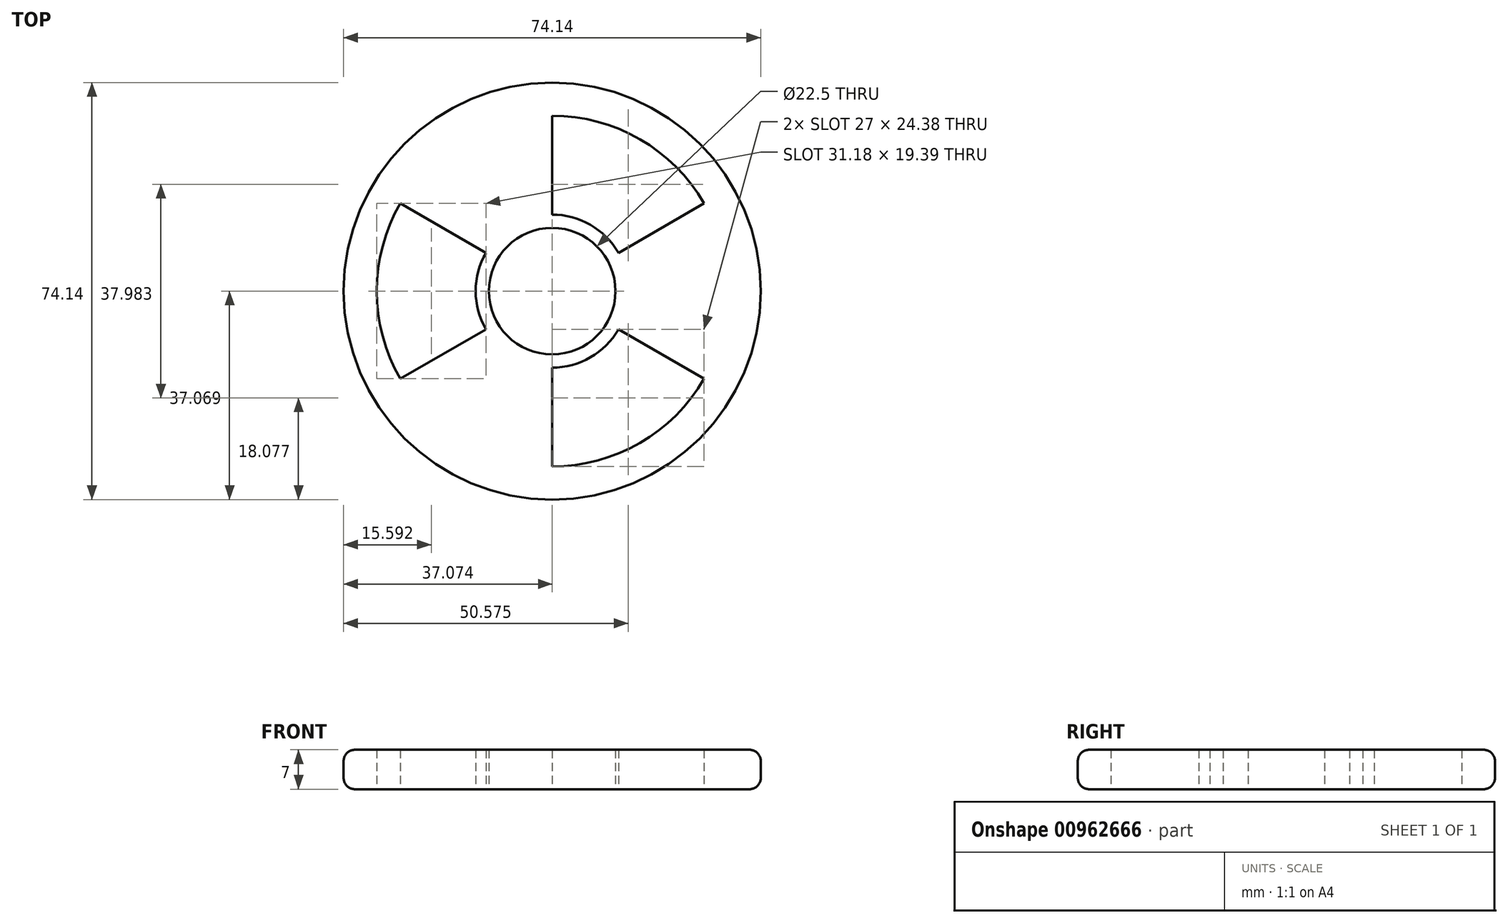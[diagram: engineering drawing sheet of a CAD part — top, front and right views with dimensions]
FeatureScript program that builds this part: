
annotation { "Feature Type Name" : "Feature", "Feature Type Description" : "" }
export const myFeature = defineFeature(function(context is Context, id is Id, definition is map)
    precondition{}
    {
        {
            var Q0;
            Q0=qCreatedBy(makeId("Top.planeOp"),FACE);
            var sketch = newSketch(context, id + "F0", { "sketchPlane" : qUnion([Q0])});
            skCircle(sketch, "E0", {"center": v(-44.39, -7.32) * mm, "radius": 11.25 * mm});
            skCircle(sketch, "E1", {"center": v(-44.39, -7.32) * mm, "radius": 37.07 * mm});
            skCircle(sketch, "E2", {"center": v(-44.39, -7.32) * mm, "radius": 31.18 * mm});
            skCircle(sketch, "E3", {"center": v(-44.39, -7.32) * mm, "radius": 13.6 * mm});
            skLineSegment(sketch, "E4", {"start": v(-44.39, 6.29) * mm, "end": v(-44.39, 23.86) * mm});
            skLineSegment(sketch, "E5.1.0", {"start": v(-56.17, -0.52) * mm, "end": v(-71.39, 8.27) * mm});
            skLineSegment(sketch, "E5.2.0", {"start": v(-56.17, -14.13) * mm, "end": v(-71.39, -22.91) * mm});
            skLineSegment(sketch, "E5.3.0", {"start": v(-44.39, -20.93) * mm, "end": v(-44.39, -38.5) * mm});
            skLineSegment(sketch, "E5.4.0", {"start": v(-32.6, -14.13) * mm, "end": v(-17.38, -22.91) * mm});
            skLineSegment(sketch, "E5.5.0", {"start": v(-32.6, -0.52) * mm, "end": v(-17.38, 8.27) * mm});
            skSolve(sketch);
        }
        {
            var Q0;
            Q0 = qSketchRegion(id + "F0", true);
            var Q1;
            Q1=makeQuery(id+"F0.imprint","IMPRINT",FACE,{"disambiguationData":[TD([[makeQuery(id+"F0.imprint","IMPRINT",EDGE,{"derivedFrom":sQuery(id+"F0.wireOp",EDGE,"E0")}),-1.0]])]});
            var Q2;
            {var subQ0=sQuery(id+"F0.wireOp",EDGE,"E5.2.0");Q2=makeQuery(id+"F0.imprint","IMPRINT",FACE,{"disambiguationData":[TD([[makeQuery(id+"F0.imprint","IMPRINT",EDGE,{"derivedFrom":subQ0}),1.0]])]});}
            var Q3;
            {var subQ0=sQuery(id+"F0.wireOp",EDGE,"E4");Q3=makeQuery(id+"F0.imprint","IMPRINT",FACE,{"disambiguationData":[TD([[makeQuery(id+"F0.imprint","IMPRINT",EDGE,{"derivedFrom":subQ0}),1.0]])]});}
            var Q4;
            {var subQ0=sQuery(id+"F0.wireOp",EDGE,"E5.4.0");Q4=makeQuery(id+"F0.imprint","IMPRINT",FACE,{"disambiguationData":[TD([[makeQuery(id+"F0.imprint","IMPRINT",EDGE,{"derivedFrom":subQ0}),1.0]])]});}
            extrude(context, id + "F1", {"entities" : qUnion([Q0, Q1, Q2, Q3, Q4]), "depth" : 7 * mm, "offsetDistance" : 25 * mm});
        }
        {
            var Q0;
            Q0=makeQuery(id+"F1.opExtrude","CAP_EDGE",EDGE,{"disambiguationData":[OSD([sQuery(id+"F0.wireOp",EDGE,"E1")])],"isStart":true});
            var Q1;
            Q1=makeQuery(id+"F1.opExtrude","CAP_EDGE",EDGE,{"disambiguationData":[OSD([sQuery(id+"F0.wireOp",EDGE,"E1")])],"isStart":false});
            fillet(context, id + "F2", {"entities" : qUnion([Q0, Q1]), "radius" : 2 * mm, "tangentPropagation" : true, "allowEdgeOverflow" : false});
        }
    });
